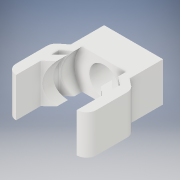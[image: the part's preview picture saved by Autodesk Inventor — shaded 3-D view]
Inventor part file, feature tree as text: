
AUTODESK INVENTOR PART (.ipt)
format: ipt  version: 2017 SP1 (Build 210196100, 196)  size: 212,992 bytes
history: native  units: in
note: dims shown in document units (in); Inventor stores cm internally (conversion verified against a paired STEP export)
features: extrude x5, sketch x5, fillet x1, projected_geometry x1
ambient origin geometry x8: Origin, YZ Plane, XZ Plane, XY Plane, X Axis, Y Axis, Z Axis, Center Point
bodies: Solid1 (feature_tree)
feature tree (12):
  extrude  "Extrusion1"  Depth=0.2362in
  extrude  "Extrusion3"  Depth=0.1575in TaperAngle=0.0deg
  fillet  "Fillet1"  Radius=0.0984in
  extrude  "Extrusion4"  Depth=0.0394in
  extrude  "Extrusion5"  Depth=0.0315in
  extrude  "Extrusion6"  Depth=0.0315in
  sketch  "Sketch1"  dims[d0=0.1181in d1=0.2362in]
  sketch  "Sketch2"  dims[d2=0.1575in d3=0.0787in d4=0.0in d5=0.0984in]
  sketch  "Sketch5"  dims[d6=0.1181in d7=0.0394in]
  sketch  "Sketch6"  dims[d8=0.1969in d11=0.0315in]
  projected_geometry  "Projected Loop3"
  sketch  "Sketch7"  dims[d13=0.1181in d15=0.0315in d18=0.0394in d19=0.1969in d20=0.0315in d21=0.1181in d22=0.0315in d23=0.1575in d24=0.0in d25=0.0394in d27=0.1575in d28=0.0in d29=0.1575in d30=0.0in d31=0.2362in d32=0.1575in d33=0.0in]
